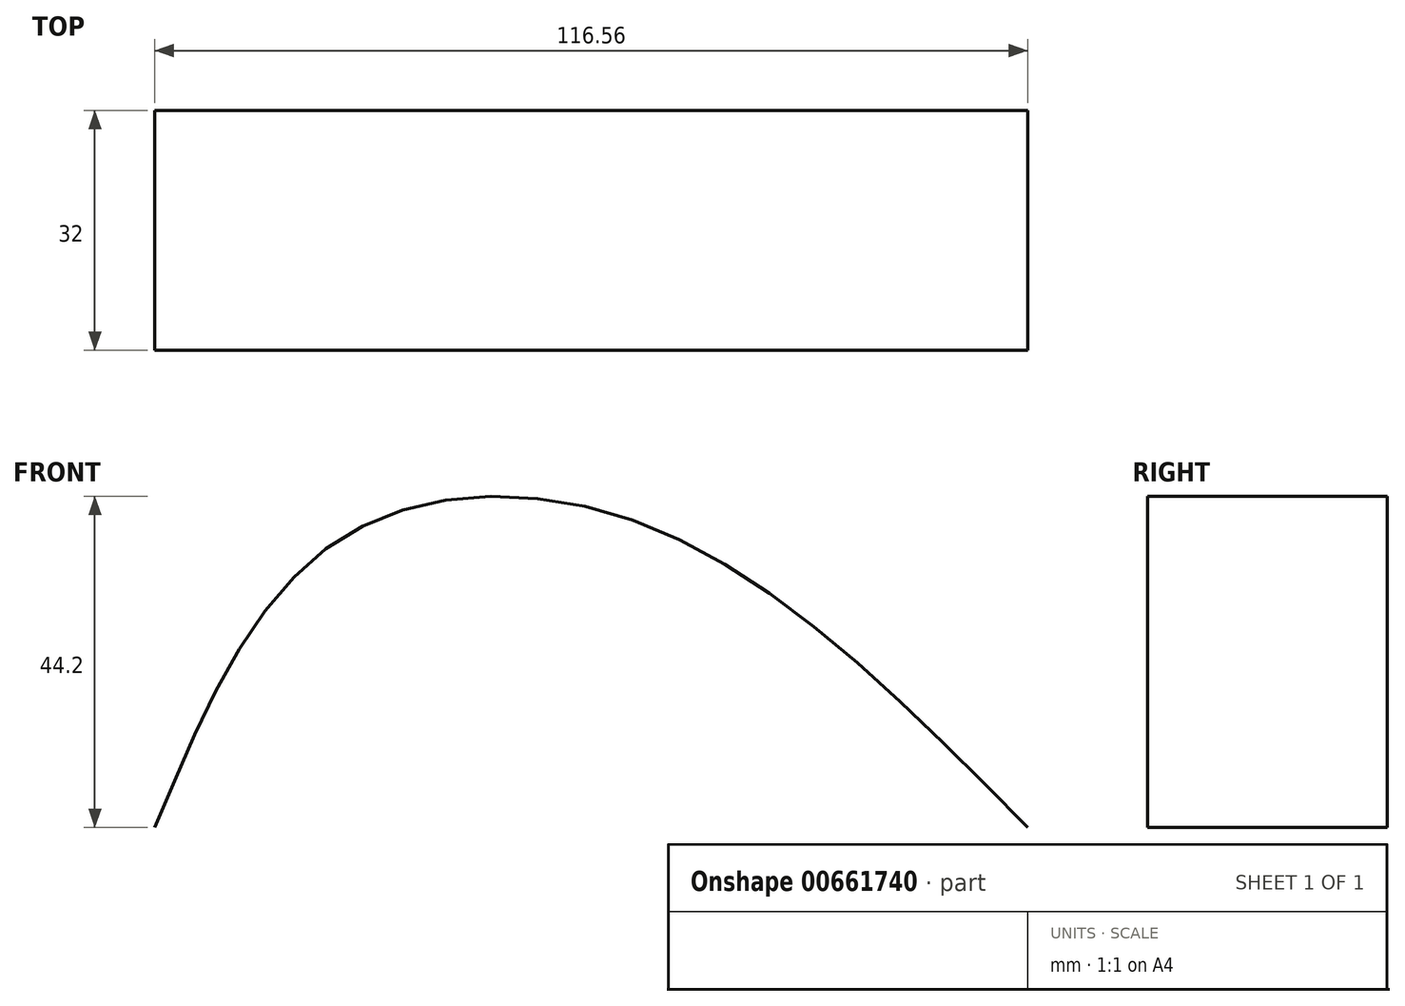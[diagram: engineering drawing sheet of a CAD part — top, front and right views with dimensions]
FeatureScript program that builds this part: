
annotation { "Feature Type Name" : "Feature", "Feature Type Description" : "" }
export const myFeature = defineFeature(function(context is Context, id is Id, definition is map)
    precondition{}
    {
        {
            var Q0;
            Q0=qCreatedBy(makeId("Front.planeOp"),FACE);
            var sketch = newSketch(context, id + "F0", { "sketchPlane" : qUnion([Q0])});
            skFitSpline(sketch, "E0", {"points": [v(-67.78, 0) * mm, v(-43.6, 38.13) * mm, v(-2.45, 40.44) * mm, v(48.78, 0) * mm], "startDerivative": vector(60.12, 144.1) * mm, "endDerivative": vector(129.83, -131.61) * mm});
            skSolve(sketch);
        }
        {
            var Q0;
            Q0=sQuery(id+"F0.wireOp",EDGE,"E0");
            extrude(context, id + "F1", {"bodyType" : ToolBodyType.SURFACE, "surfaceEntities" : qUnion([Q0]), "depth" : 32 * mm, "offsetDistance" : 25.4 * mm});
        }
    });
